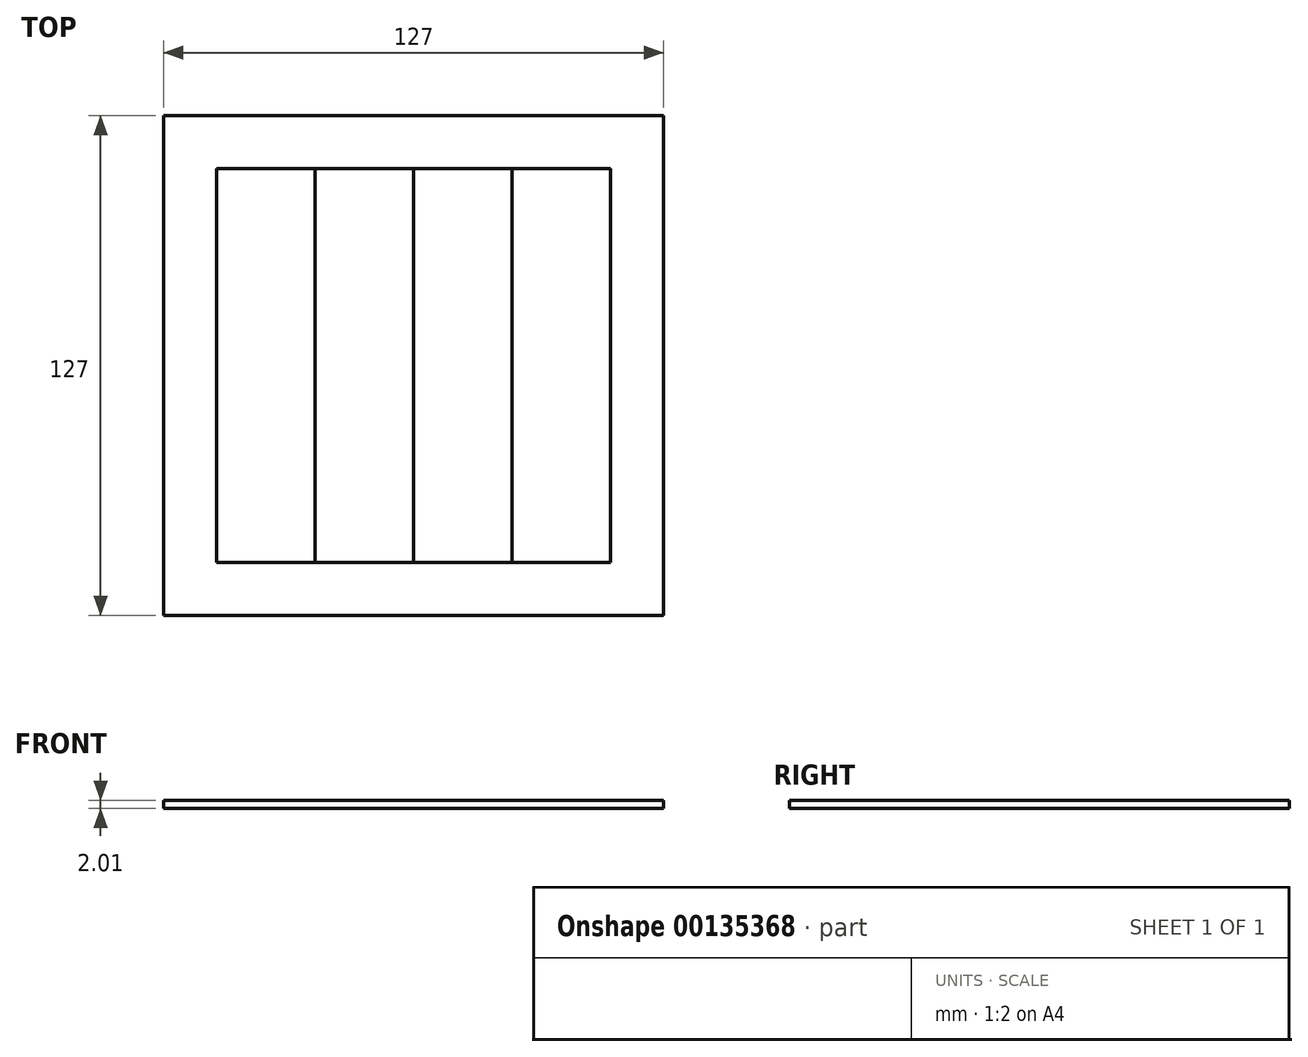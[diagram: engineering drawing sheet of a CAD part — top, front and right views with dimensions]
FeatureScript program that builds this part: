
annotation { "Feature Type Name" : "Feature", "Feature Type Description" : "" }
export const myFeature = defineFeature(function(context is Context, id is Id, definition is map)
    precondition{}
    {
        {
            var Q0;
            Q0=qCreatedBy(makeId("Top.planeOp"),FACE);
            var sketch = newSketch(context, id + "F0", { "sketchPlane" : qUnion([Q0])});
            skLineSegment(sketch, "E0.bottom", {"start": v(0, 0) * mm, "end": v(127, 0) * mm});
            skLineSegment(sketch, "E0.top", {"start": v(0, 127) * mm, "end": v(127, 127) * mm});
            skLineSegment(sketch, "E0.left", {"start": v(0, 0) * mm, "end": v(0, 127) * mm});
            skLineSegment(sketch, "E0.right", {"start": v(127, 0) * mm, "end": v(127, 127) * mm});
            skSolve(sketch);
        }
        {
            var Q0;
            Q0 = qSketchRegion(id + "F0", true);
            extrude(context, id + "F1", {"entities" : qUnion([Q0]), "depth" : 2 * mm});
        }
        {
            var Q0;
            Q0=makeQuery(id+"F1.opExtrude","CAP_FACE",FACE,{"disambiguationData":[OSD([sQuery(id+"F0.wireOp",EDGE,"E0.bottom"),sQuery(id+"F0.wireOp",EDGE,"E0.top"),sQuery(id+"F0.wireOp",EDGE,"E0.left"),sQuery(id+"F0.wireOp",EDGE,"E0.right")])],"isStart":false});
            var sketch = newSketch(context, id + "F2", { "sketchPlane" : qUnion([Q0])});
            skLineSegment(sketch, "E1.bottom", {"start": v(13.5, 113.5) * mm, "end": v(113.5, 113.5) * mm});
            skLineSegment(sketch, "E1.top", {"start": v(13.5, 13.5) * mm, "end": v(113.5, 13.5) * mm});
            skLineSegment(sketch, "E1.left", {"start": v(13.5, 113.5) * mm, "end": v(13.5, 13.5) * mm});
            skLineSegment(sketch, "E1.right", {"start": v(113.5, 113.5) * mm, "end": v(113.5, 13.5) * mm});
            skLineSegment(sketch, "E2", {"start": v(38.5, 113.5) * mm, "end": v(38.5, 13.5) * mm});
            skLineSegment(sketch, "E3", {"start": v(63.5, 113.5) * mm, "end": v(63.5, 13.5) * mm});
            skLineSegment(sketch, "E4", {"start": v(88.5, 113.5) * mm, "end": v(88.5, 13.5) * mm});
            skSolve(sketch);
        }
        {
            var Q0;
            {var subQ0=sQuery(id+"F2.wireOp",EDGE,"E1.left");Q0=makeQuery(id+"F2.imprint","IMPRINT",FACE,{"disambiguationData":[TD([[makeQuery(id+"F2.imprint","IMPRINT",EDGE,{"derivedFrom":subQ0}),1.0]])]});}
            extrude(context, id + "F3", {"entities" : qUnion([Q0]), "depth" : 0.01 * mm});
        }
        {
            var Q0;
            {var subQ0=sQuery(id+"F2.wireOp",EDGE,"E2");Q0=makeQuery(id+"F2.imprint","IMPRINT",FACE,{"disambiguationData":[TD([[makeQuery(id+"F2.imprint","IMPRINT",EDGE,{"derivedFrom":subQ0}),1.0]])]});}
            extrude(context, id + "F4", {"entities" : qUnion([Q0]), "depth" : 0.01 * mm});
        }
        {
            var Q0;
            {var subQ0=sQuery(id+"F2.wireOp",EDGE,"E3");Q0=makeQuery(id+"F2.imprint","IMPRINT",FACE,{"disambiguationData":[TD([[makeQuery(id+"F2.imprint","IMPRINT",EDGE,{"derivedFrom":subQ0}),1.0]])]});}
            extrude(context, id + "F5", {"entities" : qUnion([Q0]), "depth" : 0.01 * mm});
        }
        {
            var Q0;
            {var subQ0=sQuery(id+"F2.wireOp",EDGE,"E1.right");Q0=makeQuery(id+"F2.imprint","IMPRINT",FACE,{"disambiguationData":[TD([[makeQuery(id+"F2.imprint","IMPRINT",EDGE,{"derivedFrom":subQ0}),-1.0]])]});}
            extrude(context, id + "F6", {"entities" : qUnion([Q0]), "depth" : 0.01 * mm});
        }
    });
